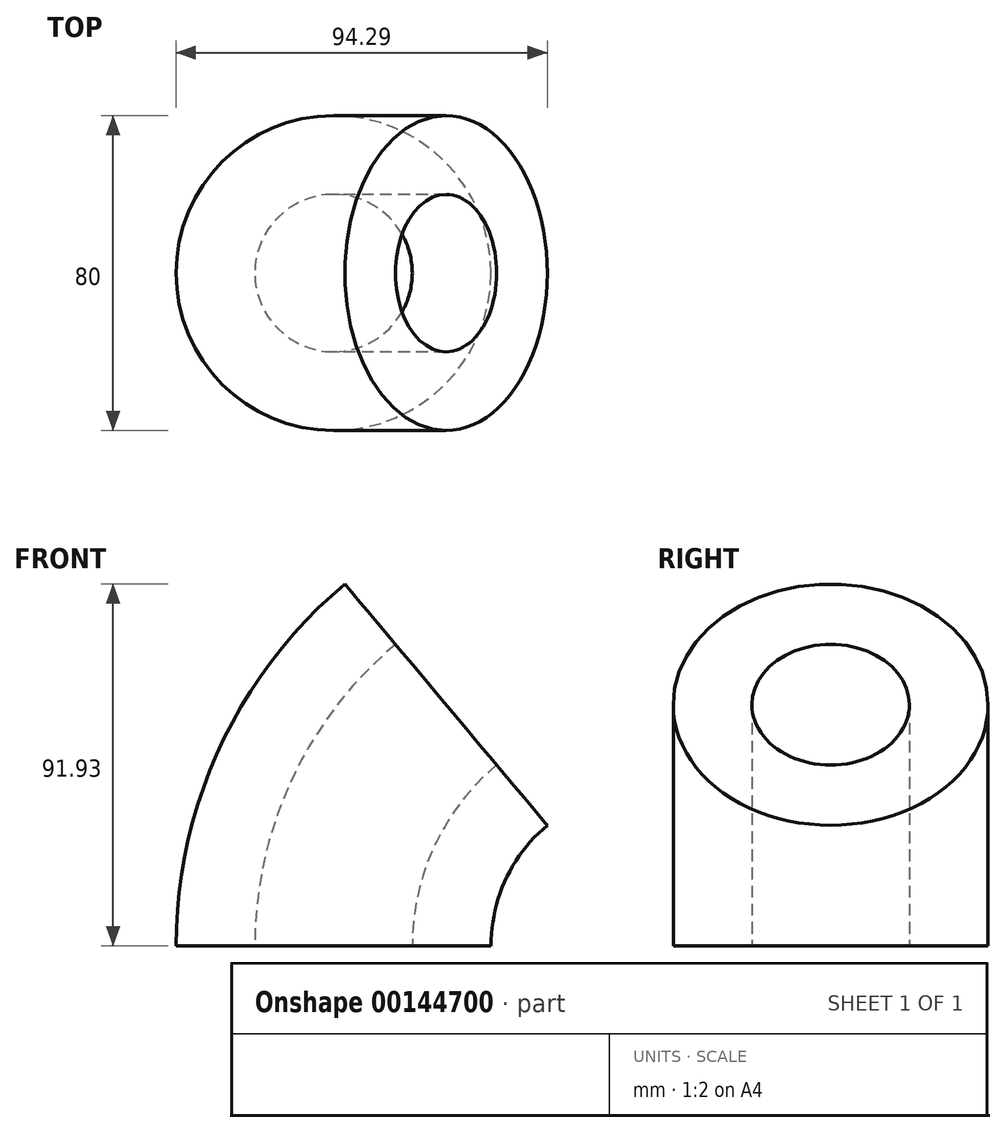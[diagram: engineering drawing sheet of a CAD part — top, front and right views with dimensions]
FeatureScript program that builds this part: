
annotation { "Feature Type Name" : "Feature", "Feature Type Description" : "" }
export const myFeature = defineFeature(function(context is Context, id is Id, definition is map)
    precondition{}
    {
        {
            assignVariable(context, id + "F0", {"name" : "kat", "anyValue" : 50});
        }
        {
            var Q0;
            Q0=qCreatedBy(makeId("Top.planeOp"),FACE);
            var sketch = newSketch(context, id + "F1", { "sketchPlane" : qUnion([Q0])});
            skCircle(sketch, "E0", {"center": v(-80, 0) * mm, "radius": 20 * mm});
            skCircle(sketch, "E1", {"center": v(-80, 0) * mm, "radius": 40 * mm});
            skLineSegment(sketch, "E2", {"start": v(0, 0) * mm, "end": v(0, -43.92) * mm});
            skSolve(sketch);
        }
        {
            var Q0;
            Q0=makeQuery(id+"F1.imprint","IMPRINT",FACE,{"disambiguationData":[TD([[makeQuery(id+"F1.imprint","IMPRINT",EDGE,{"derivedFrom":sQuery(id+"F1.wireOp",EDGE,"E0")}),-1.0]])]});
            var Q1;
            Q1=sQuery(id+"F1.wireOp",EDGE,"E2");
            revolve(context, id + "F2", {"entities" : qUnion([Q0]), "axis" : qUnion([Q1]), "revolveType" : RevolveType.ONE_DIRECTION, "oppositeDirection" : true, "angle" : (getVariable(context, 'kat')) * degree});
        }
    });
